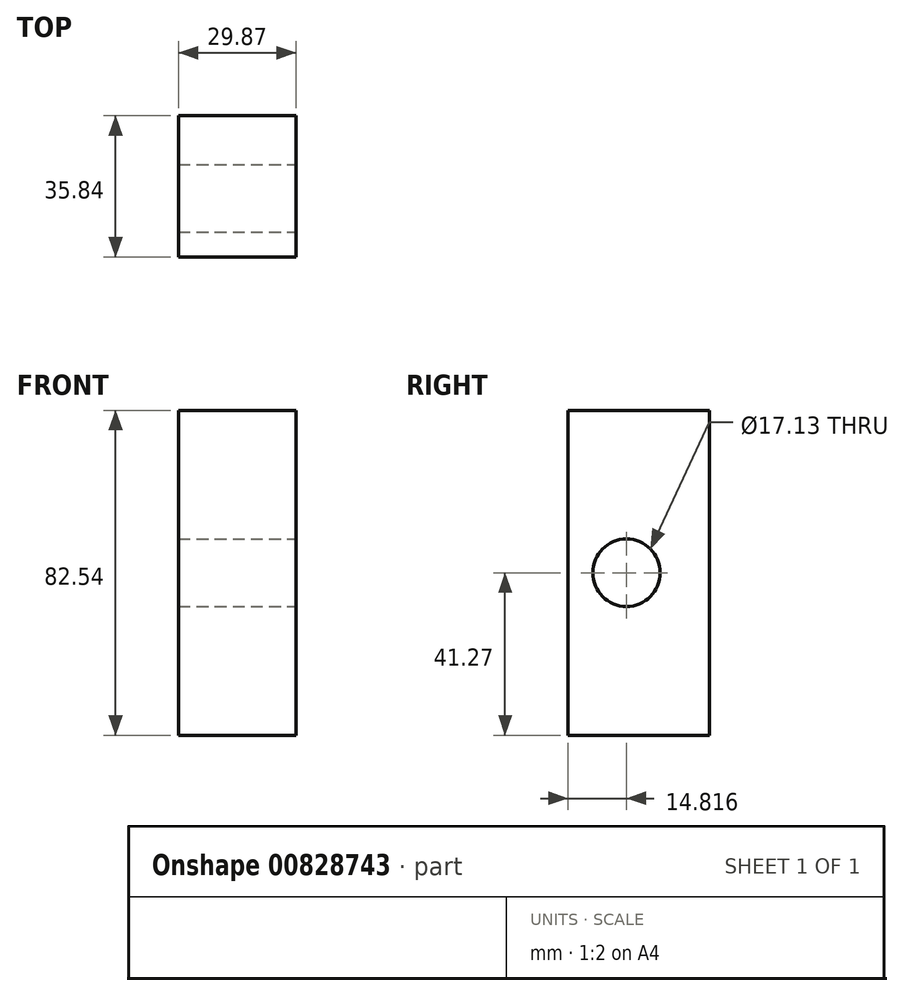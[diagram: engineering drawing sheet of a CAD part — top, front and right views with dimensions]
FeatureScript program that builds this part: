
annotation { "Feature Type Name" : "Feature", "Feature Type Description" : "" }
export const myFeature = defineFeature(function(context is Context, id is Id, definition is map)
    precondition{}
    {
        {
            var Q0;
            Q0=qCreatedBy(makeId("Front.planeOp"),FACE);
            var sketch = newSketch(context, id + "F0", { "sketchPlane" : qUnion([Q0])});
            skLineSegment(sketch, "E0.bottom", {"start": v(0, 41.27) * mm, "end": v(0, 41.27) * mm});
            skLineSegment(sketch, "E0.top", {"start": v(0, -112.09) * mm, "end": v(0, -112.09) * mm});
            skLineSegment(sketch, "E0.left", {"start": v(0, 41.27) * mm, "end": v(0, -112.09) * mm});
            skLineSegment(sketch, "E0.right", {"start": v(0, 41.27) * mm, "end": v(0, -112.09) * mm});
            skPoint(sketch, "E0.middle", {"position": v(0, -35.4) * mm});
            skLineSegment(sketch, "E1.bottom", {"start": v(46.51, 41.27) * mm, "end": v(76.38, 41.27) * mm});
            skLineSegment(sketch, "E1.top", {"start": v(46.51, -41.27) * mm, "end": v(76.38, -41.27) * mm});
            skLineSegment(sketch, "E1.left", {"start": v(46.51, 41.27) * mm, "end": v(46.51, -41.27) * mm});
            skLineSegment(sketch, "E1.right", {"start": v(76.38, 41.27) * mm, "end": v(76.38, -41.27) * mm});
            skPoint(sketch, "E1.middle", {"position": v(61.45, 0) * mm});
            skSolve(sketch);
        }
        {
            var Q0;
            Q0=makeQuery(id+"F0.imprint","IMPRINT",FACE,{"disambiguationData":[TD([[makeQuery(id+"F0.imprint","IMPRINT",EDGE,{"derivedFrom":sQuery(id+"F0.wireOp",EDGE,"E1.bottom")}),-1.0]])]});
            extrude(context, id + "F1", {"entities" : qUnion([Q0]), "depth" : 35.84 * mm, "offsetDistance" : 25.4 * mm});
        }
        {
            var Q0;
            Q0=makeQuery(id+"F1.opExtrude","SWEPT_FACE",FACE,{"disambiguationData":[OSD([sQuery(id+"F0.wireOp",EDGE,"E1.right")])]});
            var sketch = newSketch(context, id + "F2", { "sketchPlane" : qUnion([Q0])});
            skCircle(sketch, "E2", {"center": v(-21.02, 0) * mm, "radius": 8.56 * mm});
            skSolve(sketch);
        }
        {
            var Q0;
            Q0=makeQuery(id+"F2.imprint","IMPRINT",FACE,{"disambiguationData":[TD([[makeQuery(id+"F2.imprint","IMPRINT",EDGE,{"derivedFrom":sQuery(id+"F2.wireOp",EDGE,"E2")}),1.0]])]});
            var Q1;
            Q1=sQuery(id+"F2.wireOp",EDGE,"E2");
            extrude(context, id + "F3", {"entities" : qUnion([Q0]), "operationType" : NewBodyOperationType.REMOVE, "surfaceEntities" : qUnion([Q1]), "oppositeDirection" : true, "depth" : 61.74 * mm, "offsetDistance" : 25.4 * mm, "hasSecondDirection" : true, "secondDirectionOppositeDirection" : false, "secondDirectionDepth" : 25.4 * mm});
        }
    });
